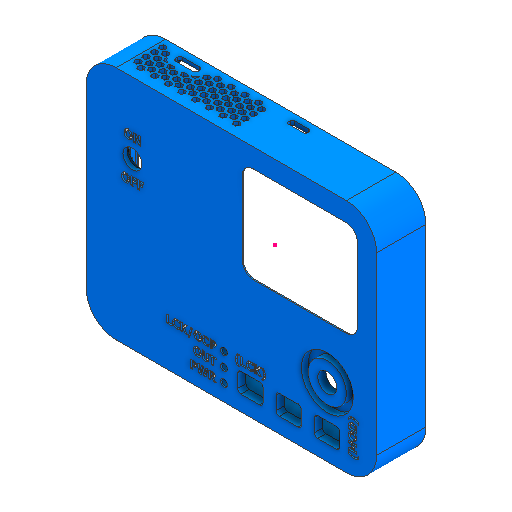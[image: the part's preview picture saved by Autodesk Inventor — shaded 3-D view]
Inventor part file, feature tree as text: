
AUTODESK INVENTOR PART (.ipt)
format: ipt  version: 2025 (Build 290162000, 162)  size: 3,690,496 bytes
history: native  units: mm
features: reference x98, sketch x43, extrude x31, other x19, fillet x6, chamfer x6, plane x4, sweep x2, mirror x2, shell x1, emboss x1, projected_geometry x1
ambient origin geometry x8: Origin, YZ Plane, XZ Plane, XY Plane, X Axis, Y Axis, Z Axis, Center Point
bodies: Solid1 (feature_tree)
feature tree (214):
  extrude  "Extrusion1"  Depth=3.0mm
  fillet  "Fillet1"  Radius=3.0mm
  shell  "Shell1"  Thickness=11.0mm
  extrude  "Extrusion_toggle"  Depth=0.3mm
  extrude  "Extrusion_encoder"  Depth=0.5mm
  extrude  "Extrusion_encoder_knob"  Depth=14.0mm
  extrude  "Extrusion_UI_BTNS"  Depth=2.6mm TaperAngle=0.0deg
  extrude  "Extrusion_Display"  Depth=2.0mm TaperAngle=0.0deg
  extrude  "Extrusion10"  Depth=10.0mm TaperAngle=0.0deg
  extrude  "Extrusion11"  Depth=3.3mm
  fillet  "Fillet4"  Radius=0.9mm
  plane  "Work Plane7"
  plane  "Work Plane8"
  extrude  "Extrusion17"  Depth=5.0mm
  extrude  "Extrusion18"  Depth=2.7mm TaperAngle=0.0deg
  sketch  "Sketch24"  dims[d107=0.25mm d108=0.0mm d109=0.3mm]
  extrude  "Extrusion19"  Depth=2.0mm
  extrude  "Extrusion20"  Depth=1.2mm
  extrude  "USB_C_1"  Depth=1.5mm TaperAngle=0.0deg
  extrude  "USB_C_2"  Depth=2.0mm TaperAngle=0.0deg
  extrude  "USB_Micro_B_1"  Depth=0.3mm
  extrude  "USB_Micro_B_2"  Depth=1.4mm TaperAngle=0.0deg
  extrude  "Venting_1"  Depth=0.25mm
  extrude  "Venting_2"  Depth=1.8mm TaperAngle=0.0deg
  sketch  "Sketch34"  dims[d142=40.0mm d144=3.0mm d145=10.0mm d147=10.0mm]
  extrude  "Extrusion27"  Depth=0.25mm
  chamfer  "Chamfer1"  Distance=1.4mm
  extrude  "Extrusion28"  Depth=7.0mm
  extrude  "Extrusion29"  TaperAngle=150.0deg  [1 undecoded]
  chamfer  "Chamfer3"  Distance=10.0mm
  extrude  "Extrusion30"  Depth=3.5mm
  extrude  "Display_hole_1"  Depth=0.3mm TaperAngle=45.0deg
  extrude  "Display_hole_2"  Depth=1.0mm
  fillet  "Fillet5"  Radius=1.0mm
  plane  "Work Plane9"
  plane  "Work Plane11"
  extrude  "Extrusion33"  Depth=0.7mm
  sweep  "Sweep2"
  chamfer  "Chamfer5"  Distance=1.8mm
  extrude  "Extrusion34"  Depth=0.7mm
  fillet  "Fillet7"  Radius=0.7mm
  chamfer  "Chamfer7"  Distance=2.5mm
  mirror  "Mirror1"
  mirror  "Mirror2"
  fillet  "Fillet8"  Radius=1.0mm
  chamfer  "Chamfer8"  Distance=1.8mm
  sketch  "Sketch44"  dims[d197=4.0mm d198=0.7mm d199=3.75mm d200=0.0mm d201=1.0mm d202=1.0mm]
  fillet  "Fillet9"  Radius=1.5mm
  sweep  "Sweep3"
  extrude  "Extrusion36"  Depth=0.4mm
  extrude  "Extrusion37"  Depth=0.4mm
  emboss  "Emboss1"
  extrude  "Extrusion38"  Depth=0.4mm
  chamfer  "Chamfer9"  Distance=4.0mm
  extrude  "Extrusion39"  Depth=0.4mm
  extrude  "Extrusion40"  Depth=0.4mm TaperAngle=0.0deg
  sketch  "Sketch1"  dims[d0=16.0mm d1=0.0mm d5=3.0mm d6=3.0mm d7=11.0mm]
  reference  "Reference1"
  reference  "Reference2"
  reference  "Reference3"
  reference  "Reference4"
  sketch  "Sketch3"  dims[d20=16.0mm d21=0.0mm d22=0.5mm]
  reference  "Reference53"
  sketch  "Sketch4"  dims[d23=16.0mm d24=0.0mm d25=14.0mm]
  reference  "Reference54"
  sketch  "Sketch5"  dims[d29=2.6mm d36=2.0mm d37=0.0mm]
  sketch  "Sketch6"  dims[d56=7.5mm d57=3.3mm d58=0.9mm]
  reference  "Reference55"
  reference  "Reference56"
  reference  "Reference57"
  reference  "Reference58"
  reference  "Reference59"
  reference  "Reference60"
  sketch  "Sketch7"  dims[d64=19.05mm d65=2.7mm d66=0.0mm]
  reference  "Reference61"
  reference  "Reference62"
  reference  "Reference63"
  reference  "Reference64"
  reference  "Reference65"
  reference  "Reference66"
  reference  "Reference67"
  reference  "Reference68"
  sketch  "Sketch10"  dims[d67=4.0mm d68=2.0mm]
  sketch  "Sketch11"  dims[d73=10.0mm d74=0.0mm d75=1.2mm]
  reference  "Reference69"
  reference  "Reference70"
  reference  "Reference71"
  sketch  "Sketch21"  dims[d101=0.5mm d102=1.5mm d103=0.0mm]
  reference  "Reference75"
  reference  "Reference76"
  reference  "Reference77"
  reference  "Reference78"
  reference  "Reference79"
  reference  "Reference80"
  reference  "Reference81"
  reference  "Reference82"
  sketch  "Sketch22"  dims[d104=1.2mm d105=2.0mm d106=0.0mm]
  reference  "Reference83"
  reference  "Reference84"
  reference  "Reference85"
  sketch  "Sketch25"  dims[d110=0.3mm d111=1.4mm d112=0.0mm]
  sketch  "Sketch26"  dims[d113=1.4mm d114=0.0mm d115=0.25mm]
  reference  "Reference86"
  reference  "Reference87"
  sketch  "Sketch27"  dims[d116=10.0mm d117=1.8mm d118=0.0mm]
  reference  "Reference88"
  reference  "Reference89"
  reference  "Reference90"
  reference  "Reference91"
  reference  "Reference92"
  reference  "Reference93"
  reference  "Reference94"
  reference  "Reference95"
  reference  "Reference96"
  sketch  "Sketch28"  dims[d119=1.8mm d120=0.0mm d121=0.25mm]
  reference  "Reference97"
  reference  "Reference98"
  reference  "Reference99"
  sketch  "Sketch29"  dims[d122=6.0mm d123=1.4mm d124=0.0mm]
  reference  "Reference100"
  reference  "Reference101"
  reference  "Reference102"
  reference  "Reference103"
  reference  "Reference104"
  reference  "Reference105"
  reference  "Reference106"
  reference  "Reference107"
  reference  "Reference108"
  reference  "Reference109"
  reference  "Reference110"
  reference  "Reference111"
  reference  "Reference112"
  reference  "Reference113"
  reference  "Reference114"
  reference  "Reference115"
  reference  "Reference116"
  reference  "Reference117"
  reference  "Reference118"
  sketch  "Sketch30"  dims[d126=3.4mm d127=7.0mm]
  reference  "Reference119"
  reference  "Reference120"
  reference  "Reference121"
  reference  "Reference122"
  sketch  "Sketch31"  dims[d136=1.4mm d137=0.0mm d138=150.0deg]
  reference  "Reference123"
  sketch  "Sketch Rectangular Pattern2"  dims[d8=3.0mm d19=0.3mm]
  sketch  "Sketch Rectangular Pattern4"  dims[d26=19.0mm d27=2.6mm d28=0.0mm]
  sketch  "Sketch33"  dims[d139=60.0deg]
  sketch  "Sketch Rectangular Pattern5"  dims[d41=10.0mm d42=10.0mm d43=0.0mm]
  sketch  "Sketch Rectangular Pattern6"  dims[d59=20.0mm d60=5.0mm]
  sketch  "Sketch35"  dims[d157=20.0mm d159=3.0mm d160=100.0mm d162=5.0mm]
  sketch  "Sketch36"  dims[d166=30.0deg]
  sketch  "Sketch37"  dims[d169=3.4mm]
  sketch  "Sketch38"  dims[d170=40.0mm d172=3.0mm d173=10.0mm d175=10.0mm]
  sketch  "Sketch39"  dims[d177=20.0mm d179=3.0mm d180=90.0mm d182=5.0mm]
  sketch  "Sketch40"  dims[d185=3.8mm]
  sketch  "Sketch41"  dims[d186=2.0mm d187=10.0mm d188=0.0mm]
  sketch  "Sketch42"  dims[d189=4.0mm d190=3.5mm]
  reference  "Reference124"
  reference  "Reference125"
  reference  "Reference126"
  projected_geometry  "Projected Loop1"
  sketch  "3D Sketch2"
  reference  "Reference127"
  reference  "Reference128"
  sketch  "Sketch43"  dims[d191=2.15mm d192=0.0mm d193=0.3mm d194=2.0mm d195=45.0deg]
  sketch  "Sketch46"  dims[d203=4.0mm d204=0.7mm]
  reference  "Reference129"
  reference  "Reference130"
  reference  "Reference131"
  reference  "Reference132"
  reference  "Reference133"
  reference  "Reference134"
  reference  "Reference135"
  reference  "Reference136"
  reference  "Reference137"
  reference  "Reference138"
  reference  "Reference139"
  reference  "Reference140"
  sketch  "Sketch47"  dims[d208=2.0mm d209=2.0mm]
  reference  "Reference141"
  reference  "Reference142"
  reference  "Reference143"
  reference  "Reference144"
  reference  "Reference145"
  reference  "Reference146"
  reference  "Reference147"
  sketch  "Sketch48"  dims[d210=2.0mm d211=1.8mm d212=0.0mm]
  sketch  "Sketch49"  dims[d213=0.3mm d214=2.0mm d215=45.0deg d216=0.7mm d217=0.7mm]
  sketch  "Sketch50"  dims[d218=0.7mm d219=2.5mm d220=0.0mm d221=1.0mm]
  reference  "Reference148"
  sketch  "3D Sketch3"
  sketch  "Sketch51"  dims[d223=2.0mm]
  sketch  "Sketch52"  dims[d225=2.0mm d229=1.8mm d230=0.0mm d231=1.5mm d233=0.8mm d234=0.0mm d238=2.0mm d241=38.0mm d242=4.0mm d243=4.0mm d244=1.8mm d245=1.0mm d246=0.0mm d249=0.05mm d250=0.0mm d251=0.0mm d252=0.2mm d253=2.0mm d254=45.0deg d255=0.23mm d256=0.23mm d257=20.071286mm d258=1.5mm d261=0.8mm d262=8.0mm d263=0.0mm d264=0.4mm d268=2.0mm d269=2.0mm d270=2.0mm d271=45.0deg d272=1.0mm d273=0.35mm d274=2.0mm d275=60.0deg d276=0.1mm d277=0.2mm d278=7.0mm d279=11.0mm d280=4.0mm d281=11.0mm d285=4.0mm d286=3.0mm d287=3.0mm d288=3.0mm d290=4.0mm d301=6.0mm d302=0.0mm d303=0.15mm d304=1.8mm d305=0.0mm d306=10.0mm d310=1.085026mm d311=2.0mm d314=2.004307mm d315=0.6mm d316=0.0mm d317=0.25mm d319=0.3mm d320=9.0mm d321=1.4mm d322=0.0mm d323=0.3mm d324=6.981317mm d325=6.981317mm d326=0.0mm d327=0.0mm d328=0.4mm d329=2.0mm d330=45.0deg d331=2.9mm d334=1.2mm d335=0.0mm d336=11.0mm d337=22.0mm d338=0.1mm d339=2.0mm d340=2.0mm d341=0.0mm d342=8.174105mm d343=6.315728mm d344=11.305971mm d345=9.927991mm d346=8.672096mm d347=18.531031mm d348=1.0mm d349=0.3mm d351=3.080348mm d352=1.0mm d353=3.843675mm d354=3.3mm d355=13.2mm d332=0.5mm d333=0.872665mm]
  reference  "Reference149"
  other  "USB_C_PD_PPS_sink_with_enclosure.iam"
  other  "USB_C_PD_PPS_sink:1"
  other  "USB_C_PD_PPS_sink_BOARD:1"
  other  "1M41T1B5M1QE_1M41T1B5M1QE-1:1"
  other  "FP-PEC12R-4125F-S0012-MFG_CMP-07421-000016-1:1"
  other  "B3F-1052_B3F-1052-1:2"
  other  "B3F-1052_B3F-1052-1:1"
  other  "B3F-1052_B3F-1052-1:3"
  other  "VLP-600-F_VLP-600-F-1:2"
  other  "VLP-600-F_VLP-600-F-1:3"
  other  "VLP-600-F_VLP-600-F-1:1"
  other  "3461AS_3461AS-1:2"
  other  "3461AS_3461AS-1:1"
  other  "bottom_enclosure:1"
  other  "FP-USB4085-GF-A-MFG_USB4085-GF-A-1:1"
  other  "USB-MICRO-B_V_CMP-2000-05827-1:1"
  other  "display_cover_2:1"
  other  "Button cap:1"
  other  "Button cap:3"
note: 1 required parameter value undecoded (feature->parameter linkage not recoverable at this tier; creation-order binding heuristic only, values carry confidence <= 0.55)
